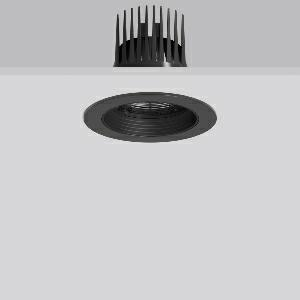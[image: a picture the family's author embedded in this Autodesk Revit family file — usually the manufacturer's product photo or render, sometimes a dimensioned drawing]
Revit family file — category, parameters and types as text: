
# Revit family: heledon_maxi_e_901768_003_76_d590
name_source: partatom
category: Lighting Fixtures
units: mm (PartAtom-declared; Revit-internal decimal feet)

## family parameters
Cut with Voids When Loaded = No
Host = Face
Light Source = No
Part Type = Normal
Room Calculation Point = No
Round Connector Dimension = Use Diameter
Shared = No

## types (1)
- HELEDON maxi E (1 x LED Modul 930, 3500 lm, 3000)
    Apparent Load = 35 VA
    Approval mark = CE
    CIE Flux Codes = 96 100 100 100 100
    Color Rendering = 90
    Color Temperature = 3000
    Default Elevation = 1800 mm
    Description = Series: HELEDON maxi
Round recessed downlight. Housing: die-cast aluminium, powder-coated. Black plastic ring and recessed LED to prevent glare from the side. Optical assembly with lens made of plastic (polycarbonate) for the best homogeneous light distribution - can be changed without tools. Best colour rendering index Ra>90. Suitable for Recessed ceiling mounting. Installation without tools thanks to spring fastening system. Including separate LED converter with connecting cable 600 mm.High quality converter without flickering and stroboscopic effect. Through-wiring box (5 pole) available as accessory. The following accessories can be mounted without use of tools: interchangeable lenses, decorative glasses, honeycomb louvre, clear and frosted diffusers, white interchangeable plastic ring. 
Colour: deep black, matt (RAL 9005)
Diameter: 162 mm
Height: 3 mm
Cut-out diameter: 152 mm
Recess height: 200 mm
Luminaire: recess height: 135 mm
Lamp: LED
Socket: without socket
Colour temperature: 3000K
Colour rendering index (CRI): 92
System power: 35 W
Rated luminous flux: 3500 lm
Luminous efficiency: 100 lm/W
Control gear: Converter, dimmable, DALI
Protection class: II
Type of protection: IP 20
    Height = 0 mm  [stored 0 ft]
    Lamp = 1 x LED Modul 930
    Lamp Light Flux = 3500 lm
    Lamp count = 1
    Length = 162 mm
    Lifetime = 50000 h
    Luminous efficacy = 100 lm/W
    Manufacturer = RZB
    ModVariant = No
    Model = 901768.003.76
    Mounting Place = Ceiling
    Mounting Type = Recessed
    Number of Poles = 1
    OnlyDefault = Yes
    Power Factor = 1
    Product Name = HELEDON maxi E
    Product group = Recessed downlights
    ProductGroupID = 402
    Protection Class = Protection class II
    Protection Degree = IP 20
    RLX_Detail_Level = 1
    RLX_Emergency_Light_Flux = 0 lm
    RLX_Emergency_Type = 0
    RLX_Emergency_Type_DB = No
    RlxData = <blob elided: 122549 chars, md5=5428d848>
    Socket = socket
    Standby Power = 0 W
    System Light Flux = 3500 lm
    System Power = 35 W
    Type Comments = Product without accessories
    Type Image = 901663.003.jpg
    URL = http://relux.com
    VarID = ---
    Voltage = 230 V
    Voltage Range = 220-240 V
    Weight = 0.00 kg
    Width = 0 mm  [stored 0 ft]

note: [stored X ft] marks values corroborated as IEEE doubles in the binary element streams (Revit-internal decimal feet)

## geometry (parser evidence)
native form markers: Blend x4, Sweep x11
no freeform markers — native parametric forms only
